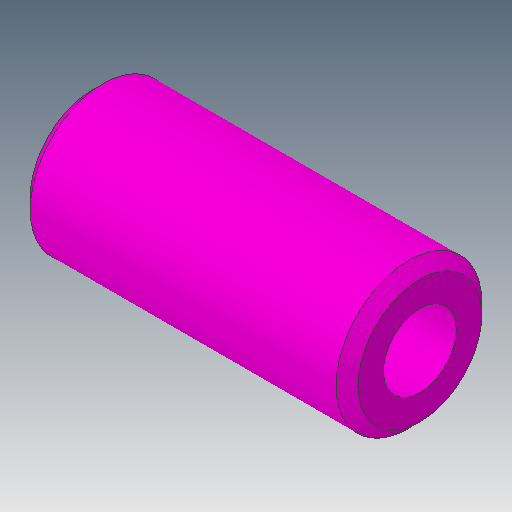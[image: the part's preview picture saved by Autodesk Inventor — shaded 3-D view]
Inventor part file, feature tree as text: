
AUTODESK INVENTOR PART (.ipt)
format: ipt  version: 2019.4 (Build 234330000, 330)  size: 107,520 bytes
history: native  units: mm
features: other x1, extrude x1, chamfer x1, sketch x1
ambient origin geometry x8: Origin, YZ Plane, XZ Plane, XY Plane, X Axis, Y Axis, Z Axis, Center Point
bodies: Body1 (feature_tree)
feature tree (4):
  other  "ソリッド1"
  extrude  "押し出し1"  Depth=4.0mm
  chamfer  "面取り1"  Distance=2.0mm
  sketch  "スケッチ1"
